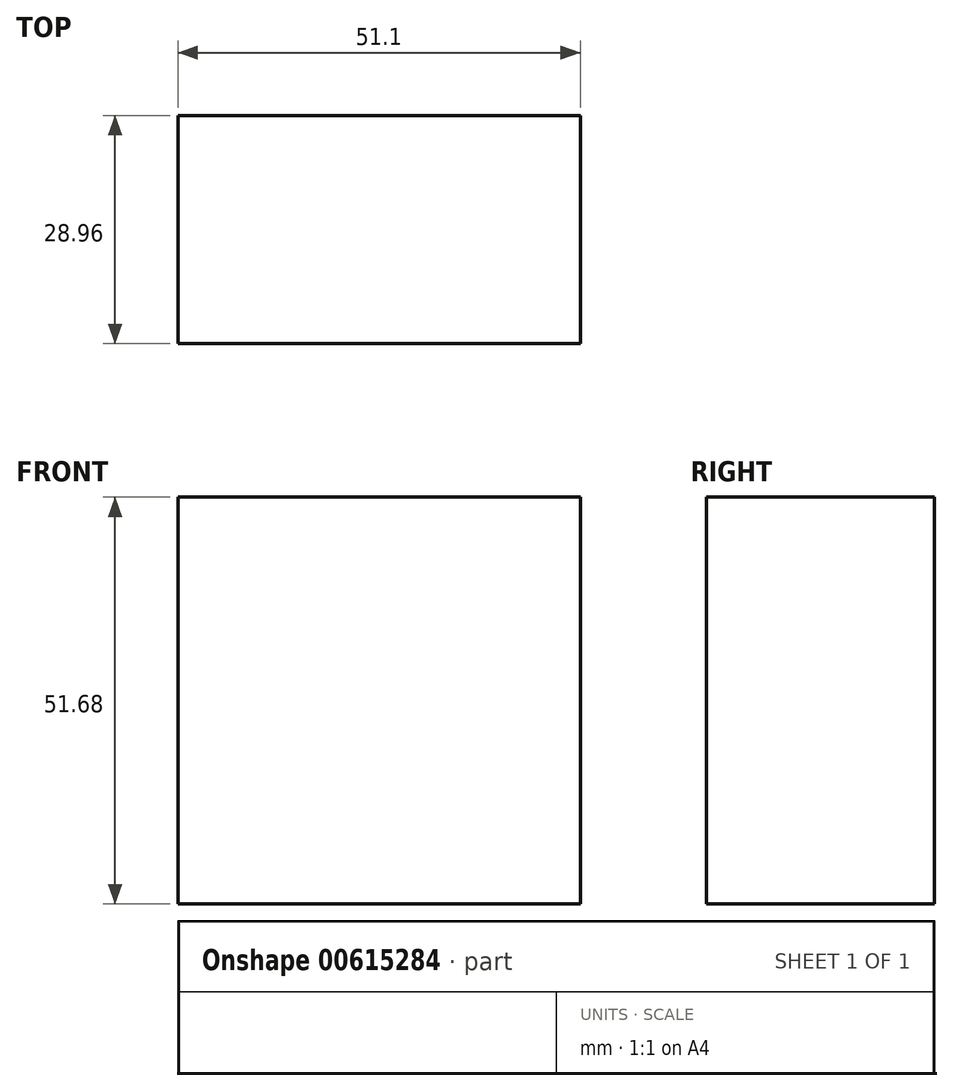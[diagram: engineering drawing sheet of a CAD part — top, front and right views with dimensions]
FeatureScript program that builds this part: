
annotation { "Feature Type Name" : "Feature", "Feature Type Description" : "" }
export const myFeature = defineFeature(function(context is Context, id is Id, definition is map)
    precondition{}
    {
        {
            var Q0;
            Q0=qCreatedBy(makeId("Front.planeOp"),FACE);
            var sketch = newSketch(context, id + "F0", { "sketchPlane" : qUnion([Q0])});
            skLineSegment(sketch, "E0.bottom", {"start": v(-25.84, 25.55) * mm, "end": v(25.26, 25.55) * mm});
            skLineSegment(sketch, "E0.top", {"start": v(-25.84, -26.13) * mm, "end": v(25.26, -26.13) * mm});
            skLineSegment(sketch, "E0.left", {"start": v(-25.84, 25.55) * mm, "end": v(-25.84, -26.13) * mm});
            skLineSegment(sketch, "E0.right", {"start": v(25.26, 25.55) * mm, "end": v(25.26, -26.13) * mm});
            skSolve(sketch);
        }
        {
            var Q0;
            Q0 = qSketchRegion(id + "F0", true);
            extrude(context, id + "F1", {"entities" : qUnion([Q0]), "depth" : 28.96 * mm, "offsetDistance" : 25.4 * mm});
        }
    });
